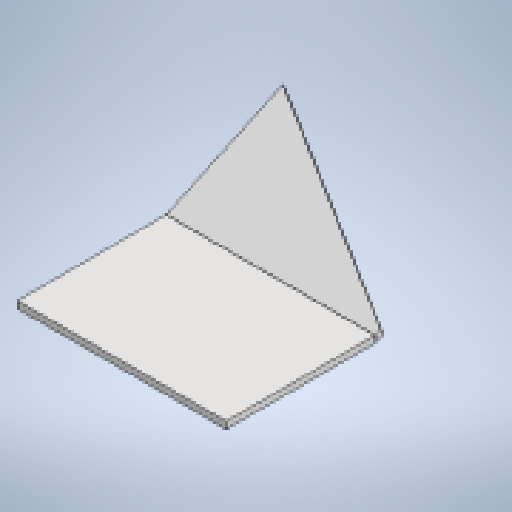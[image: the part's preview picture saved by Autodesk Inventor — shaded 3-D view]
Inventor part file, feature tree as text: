
AUTODESK INVENTOR PART (.ipt)
format: ipt  version: 2025.1 (Build 291241020, 241B)  size: 183,808 bytes
history: native  units: mm
features: sheet_metal_op x2, sketch x2, other x2, projected_geometry x1
ambient origin geometry x8: Origin, YZ Plane, XZ Plane, XY Plane, X Axis, Y Axis, Z Axis, Center Point
bodies: Body1 (feature_tree)
feature tree (7):
  sheet_metal_op  "Face2"
  sheet_metal_op  "Fold1"
  sketch  "Sketch3"  dims[d18=10.0mm]
  other  "Plate3"
  sketch  "Sketch4"  dims[d19=310.0mm d22=10.0mm d23=10.0mm d24=5.0mm d25=20.0mm d26=10.0mm d27=4.363323mm d28=1.0mm d29=232.0mm d30=182.0mm]
  projected_geometry  "Projected Loop1"
  other  "Definition1"
